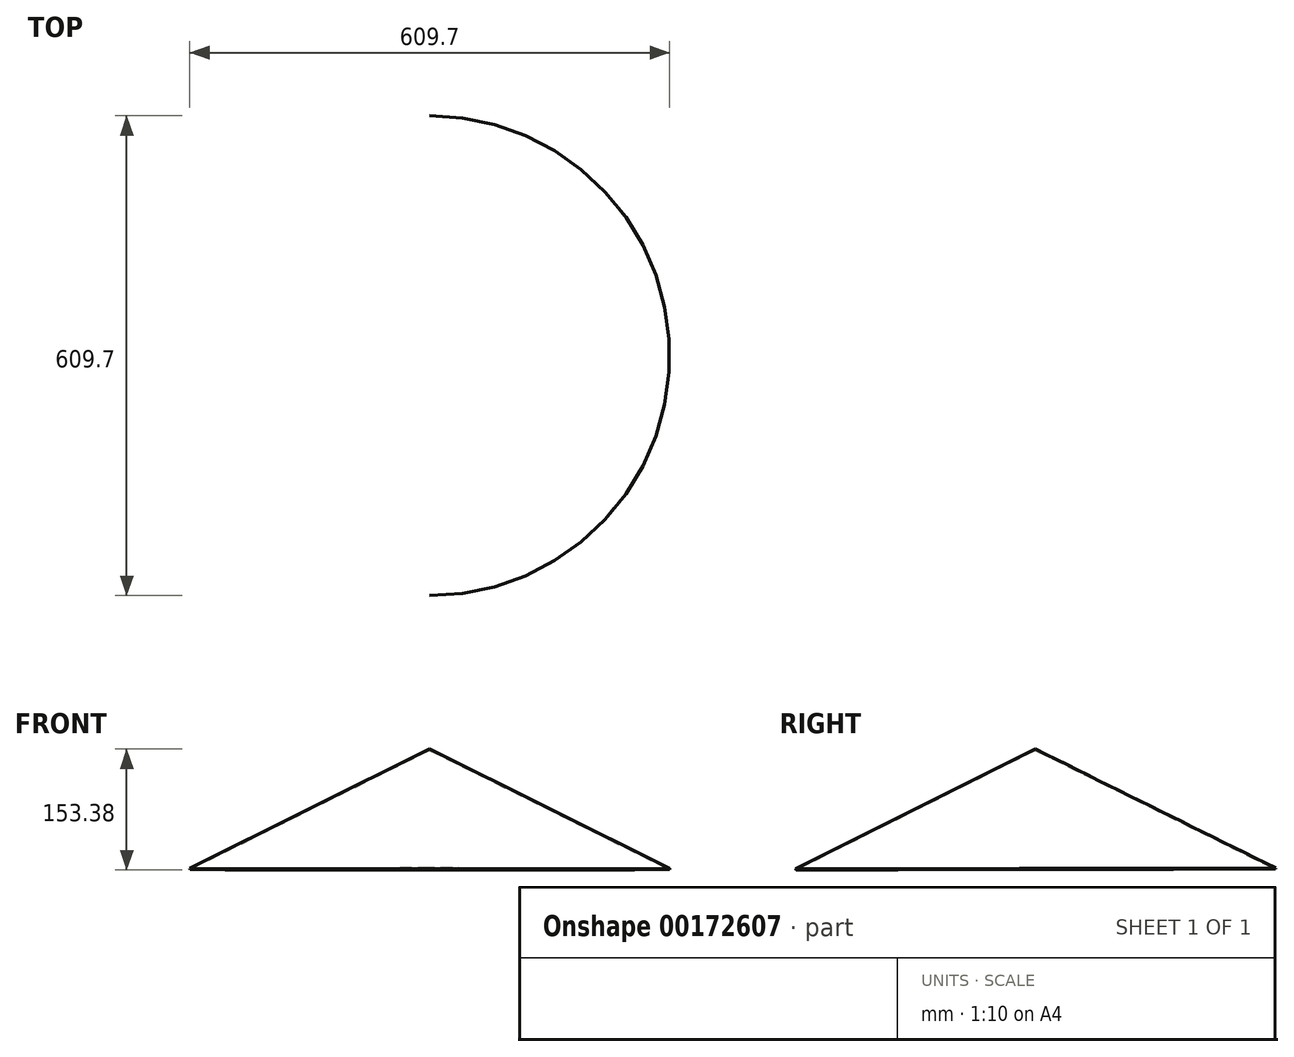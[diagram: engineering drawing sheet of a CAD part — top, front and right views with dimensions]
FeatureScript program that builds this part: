
annotation { "Feature Type Name" : "Feature", "Feature Type Description" : "" }
export const myFeature = defineFeature(function(context is Context, id is Id, definition is map)
    precondition{}
    {
        {
            var Q0;
            Q0=qCreatedBy(makeId("Right.planeOp"),FACE);
            var sketch = newSketch(context, id + "F0", { "sketchPlane" : qUnion([Q0])});
            skLineSegment(sketch, "E0", {"start": v(-0.27, 152.4) * mm, "end": v(-304.85, 0.1) * mm});
            skLineSegment(sketch, "E1", {"start": v(-304.85, 0.1) * mm, "end": v(-304.3, -0.98) * mm});
            skLineSegment(sketch, "E2", {"start": v(-0.27, 152.4) * mm, "end": v(0.27, 151.3) * mm});
            skLineSegment(sketch, "E3", {"start": v(0.27, 151.3) * mm, "end": v(-304.3, -0.98) * mm});
            skLineSegment(sketch, "E4", {"start": v(-0.27, 152.4) * mm, "end": v(0, 0) * mm});
            skPoint(sketch, "E4.endSnap0", {"position": v(0, 151.85) * mm});
            skSolve(sketch);
        }
        {
            var Q0;
            {var subQ0=sQuery(id+"F0.wireOp",EDGE,"E0");Q0=makeQuery(id+"F0.imprint","IMPRINT",FACE,{"disambiguationData":[TD([[makeQuery(id+"F0.imprint","IMPRINT",EDGE,{"derivedFrom":subQ0}),1.0]])]});}
            var Q1;
            {var subQ0=sQuery(id+"F0.wireOp",EDGE,"be2db6fa-5232-441e-9fb6-13df535d639f");Q1=makeQuery(id+"F0.imprint","IMPRINT",FACE,{"disambiguationData":[TD([[makeQuery(id+"F0.imprint","IMPRINT",EDGE,{"derivedFrom":subQ0}),1.0]])]});}
            var Q2;
            Q2=sQuery(id+"F0.wireOp",EDGE,"E4");
            revolve(context, id + "F1", {"entities" : qUnion([Q0, Q1]), "axis" : qUnion([Q2]), "revolveType" : RevolveType.FULL});
        }
    });
